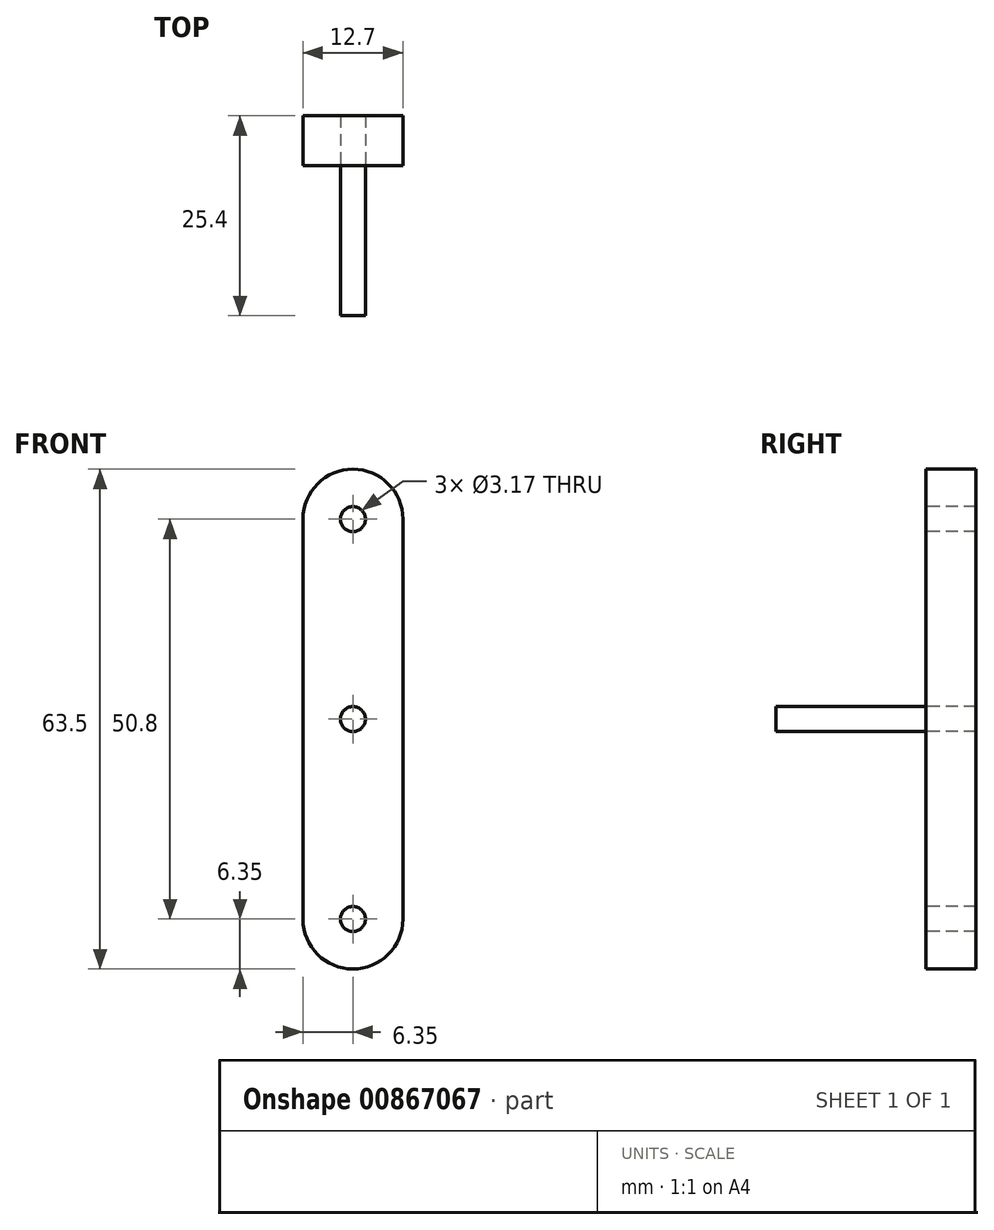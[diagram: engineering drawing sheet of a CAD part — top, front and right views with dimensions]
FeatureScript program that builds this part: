
annotation { "Feature Type Name" : "Feature", "Feature Type Description" : "" }
export const myFeature = defineFeature(function(context is Context, id is Id, definition is map)
    precondition{}
    {
        {
            var Q0;
            Q0=qCreatedBy(makeId("Front.planeOp"),FACE);
            var sketch = newSketch(context, id + "F0", { "sketchPlane" : qUnion([Q0])});
            skLineSegment(sketch, "E0", {"start": v(0, 0) * mm, "end": v(0, 50.8) * mm});
            skLineSegment(sketch, "E1", {"start": v(12.7, 0) * mm, "end": v(12.7, 50.8) * mm});
            skArc(sketch, "E2", {"start": v(12.7, 50.8) * mm, "mid": v(6.35, 57.15) * mm, "end": v(0, 50.8) * mm});
            skArc(sketch, "E3", {"start": v(0, 0) * mm, "mid": v(6.35, -6.35) * mm, "end": v(12.7, 0) * mm});
            skSolve(sketch);
        }
        {
            var Q0;
            Q0 = qSketchRegion(id + "F0", true);
            extrude(context, id + "F1", {"entities" : qUnion([Q0]), "depth" : 6.35 * mm, "offsetDistance" : 25.4 * mm});
        }
        {
            var Q0;
            Q0=makeQuery(id+"F1.opExtrude","CAP_FACE",FACE,{"disambiguationData":[OSD([sQuery(id+"F0.wireOp",EDGE,"E0"),sQuery(id+"F0.wireOp",EDGE,"E1"),sQuery(id+"F0.wireOp",EDGE,"E2"),sQuery(id+"F0.wireOp",EDGE,"E3")])],"isStart":false});
            var sketch = newSketch(context, id + "F2", { "sketchPlane" : qUnion([Q0])});
            skCircle(sketch, "E4", {"center": v(6.35, 50.8) * mm, "radius": 1.59 * mm});
            skCircle(sketch, "E5", {"center": v(6.35, 0) * mm, "radius": 1.59 * mm});
            skCircle(sketch, "E6", {"center": v(6.35, 25.4) * mm, "radius": 1.59 * mm});
            skPoint(sketch, "E6.centerSnap0", {"position": v(0, 25.4) * mm});
            skSolve(sketch);
        }
        {
            var Q0;
            Q0 = qSketchRegion(id + "F2", true);
            extrude(context, id + "F3", {"entities" : qUnion([Q0]), "operationType" : NewBodyOperationType.REMOVE, "endBound" : BoundingType.UP_TO_NEXT, "oppositeDirection" : true, "depth" : 25.4 * mm, "offsetDistance" : 25.4 * mm});
        }
        {
            var Q0;
            Q0=makeQuery(id+"F1.opExtrude","CAP_FACE",FACE,{"disambiguationData":[OSD([sQuery(id+"F0.wireOp",EDGE,"E0"),sQuery(id+"F0.wireOp",EDGE,"E1"),sQuery(id+"F0.wireOp",EDGE,"E2"),sQuery(id+"F0.wireOp",EDGE,"E3")])],"isStart":false});
            var sketch = newSketch(context, id + "F4", { "sketchPlane" : qUnion([Q0])});
            skCircle(sketch, "E7", {"center": v(6.35, 25.4) * mm, "radius": 1.59 * mm});
            skSolve(sketch);
        }
        {
            var Q0;
            Q0 = qSketchRegion(id + "F4", true);
            extrude(context, id + "F5", {"entities" : qUnion([Q0]), "depth" : 19.05 * mm, "offsetDistance" : 25.4 * mm});
        }
    });
